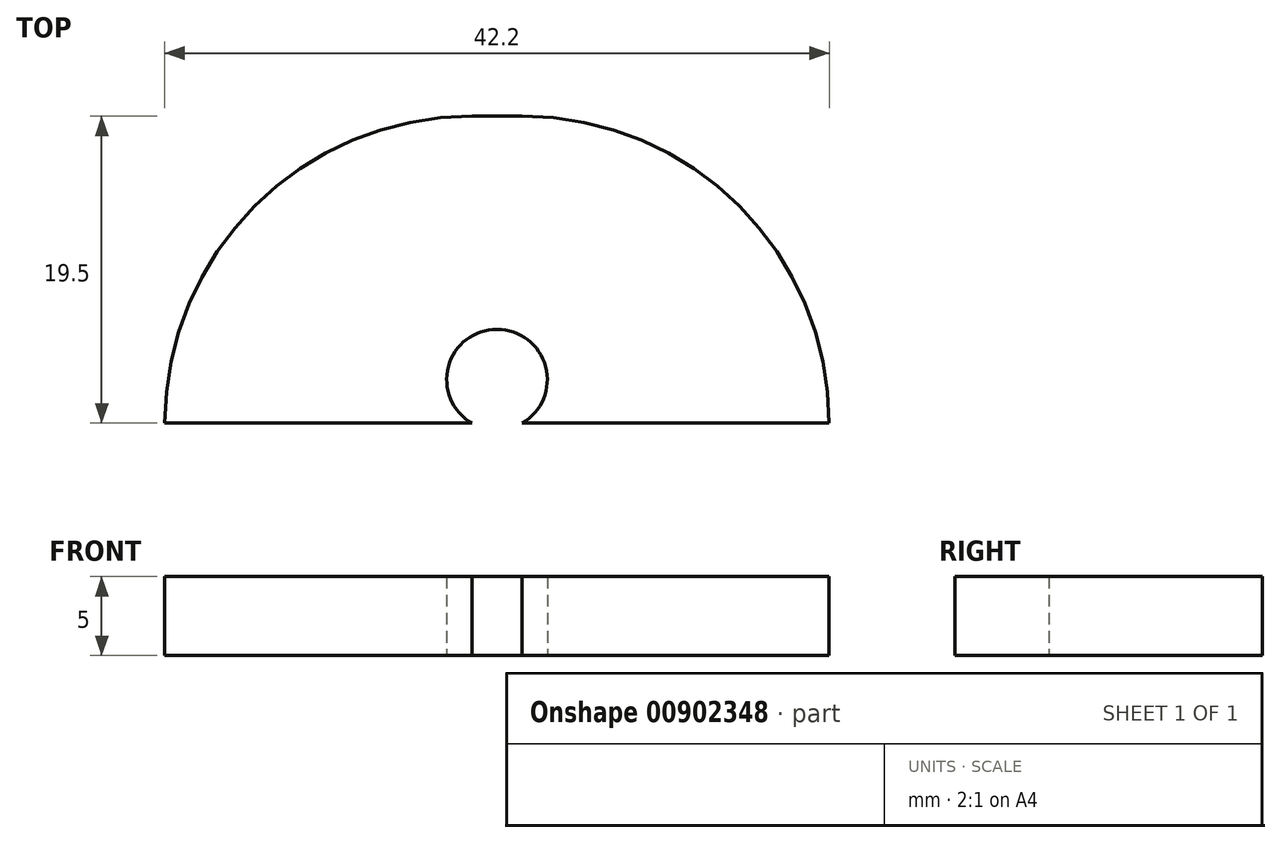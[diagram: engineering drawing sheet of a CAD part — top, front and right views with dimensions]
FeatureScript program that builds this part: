
annotation { "Feature Type Name" : "Feature", "Feature Type Description" : "" }
export const myFeature = defineFeature(function(context is Context, id is Id, definition is map)
    precondition{}
    {
        {
            var Q0;
            Q0=qCreatedBy(makeId("Top.planeOp"),FACE);
            var sketch = newSketch(context, id + "F0", { "sketchPlane" : qUnion([Q0])});
            skLineSegment(sketch, "E0.bottom", {"start": v(1.6, -9.75) * mm, "end": v(-1.6, -9.75) * mm});
            skLineSegment(sketch, "E0.top", {"start": v(1.6, 9.75) * mm, "end": v(-1.6, 9.75) * mm});
            skLineSegment(sketch, "E0.left", {"start": v(1.6, -9.75) * mm, "end": v(1.6, 9.75) * mm});
            skLineSegment(sketch, "E0.right", {"start": v(-1.6, -9.75) * mm, "end": v(-1.6, 9.75) * mm});
            skPoint(sketch, "E0.middle", {"position": v(0, 0) * mm});
            skCircle(sketch, "E1", {"center": v(1.6, -9.75) * mm, "radius": 19.5 * mm});
            skCircle(sketch, "E2", {"center": v(-1.6, -9.75) * mm, "radius": 19.5 * mm});
            skLineSegment(sketch, "E3", {"start": v(12.38, -9.75) * mm, "end": v(21.1, -9.75) * mm});
            skLineSegment(sketch, "E4", {"start": v(21.1, -9.75) * mm, "end": v(-21.1, -9.75) * mm});
            skLineSegment(sketch, "E5", {"start": v(-1.6, -9.75) * mm, "end": v(-1.6, -35.21) * mm});
            skLineSegment(sketch, "E6", {"start": v(1.6, -9.75) * mm, "end": v(1.6, -35.21) * mm});
            skLineSegment(sketch, "E7", {"start": v(21.1, -9.75) * mm, "end": v(69.98, -9.75) * mm});
            skLineSegment(sketch, "E8", {"start": v(69.98, -9.75) * mm, "end": v(-43.53, -9.75) * mm});
            skCircle(sketch, "E9", {"center": v(1.6, -9.75) * mm, "radius": 3.2 * mm});
            skCircle(sketch, "E10", {"center": v(-1.6, -9.75) * mm, "radius": 3.2 * mm});
            skCircle(sketch, "E11", {"center": v(0, -6.98) * mm, "radius": 3.2 * mm});
            skSolve(sketch);
        }
        {
            var Q0;
            {var subQ1=sQuery(id+"F0.wireOp",EDGE,"E0.right");var subQ3=sQuery(id+"F0.wireOp",EDGE,"E1");var subQ4=makeQuery(id+"F0.imprint","INTERSECT",VERTEX,{"derivedFrom":[subQ1,subQ3]});Q0=makeQuery(id+"F0.imprint","IMPRINT",FACE,{"disambiguationData":[TD([[makeQuery(id+"F0.imprint","IMPRINT",EDGE,{"disambiguationData":[TD([[subQ4,-1.0]])],"derivedFrom":subQ3}),-1.0]])]});}
            var Q1;
            {var subQ3=sQuery(id+"F0.wireOp",EDGE,"E11");var subQ7=sQuery(id+"F0.wireOp",EDGE,"E0.right");var subQ8=makeQuery(id+"F0.imprint","INTERSECT",VERTEX,{"derivedFrom":[subQ7,subQ3]});Q1=makeQuery(id+"F0.imprint","IMPRINT",FACE,{"disambiguationData":[TD([[makeQuery(id+"F0.imprint","IMPRINT",EDGE,{"disambiguationData":[TD([[subQ8,-1.0]])],"derivedFrom":subQ7}),1.0]])]});}
            var Q2;
            {var subQ1=sQuery(id+"F0.wireOp",EDGE,"E0.left");var subQ3=sQuery(id+"F0.wireOp",EDGE,"E2");var subQ4=makeQuery(id+"F0.imprint","INTERSECT",VERTEX,{"derivedFrom":[subQ1,subQ3]});Q2=makeQuery(id+"F0.imprint","IMPRINT",FACE,{"disambiguationData":[TD([[makeQuery(id+"F0.imprint","IMPRINT",EDGE,{"disambiguationData":[TD([[subQ4,1.0]])],"derivedFrom":subQ3}),-1.0]])]});}
            var Q3;
            {var subQ6=sQuery(id+"F0.wireOp",EDGE,"E0.left");var subQ9=sQuery(id+"F0.wireOp",EDGE,"E11");var subQ10=makeQuery(id+"F0.imprint","INTERSECT",VERTEX,{"derivedFrom":[subQ6,subQ9]});Q3=makeQuery(id+"F0.imprint","IMPRINT",FACE,{"disambiguationData":[TD([[makeQuery(id+"F0.imprint","IMPRINT",EDGE,{"disambiguationData":[TD([[subQ10,-1.0]])],"derivedFrom":subQ6}),-1.0]])]});}
            var Q4;
            {var subQ1=sQuery(id+"F0.wireOp",EDGE,"E4");var subQ3=sQuery(id+"F0.wireOp",EDGE,"E9");var subQ4=makeQuery(id+"F0.imprint","INTERSECT",VERTEX,{"derivedFrom":[subQ1,subQ3]});Q4=makeQuery(id+"F0.imprint","IMPRINT",FACE,{"disambiguationData":[TD([[makeQuery(id+"F0.imprint","IMPRINT",EDGE,{"disambiguationData":[TD([[subQ4,-1.0]])],"derivedFrom":subQ3}),1.0]])]});}
            var Q5;
            {var subQ1=sQuery(id+"F0.wireOp",EDGE,"E4");var subQ3=sQuery(id+"F0.wireOp",EDGE,"E10");var subQ4=makeQuery(id+"F0.imprint","INTERSECT",VERTEX,{"derivedFrom":[subQ1,subQ3]});Q5=makeQuery(id+"F0.imprint","IMPRINT",FACE,{"disambiguationData":[TD([[makeQuery(id+"F0.imprint","IMPRINT",EDGE,{"disambiguationData":[TD([[subQ4,1.0]])],"derivedFrom":subQ3}),1.0]])]});}
            var Q6;
            {var subQ1=sQuery(id+"F0.wireOp",EDGE,"E0.left");var subQ3=sQuery(id+"F0.wireOp",EDGE,"E2");var subQ4=makeQuery(id+"F0.imprint","INTERSECT",VERTEX,{"derivedFrom":[subQ1,subQ3]});Q6=makeQuery(id+"F0.imprint","IMPRINT",FACE,{"disambiguationData":[TD([[makeQuery(id+"F0.imprint","IMPRINT",EDGE,{"disambiguationData":[TD([[subQ4,-1.0]])],"derivedFrom":subQ3}),-1.0]])]});}
            var Q7;
            {var subQ1=sQuery(id+"F0.wireOp",EDGE,"E0.right");var subQ3=sQuery(id+"F0.wireOp",EDGE,"E1");var subQ4=makeQuery(id+"F0.imprint","INTERSECT",VERTEX,{"derivedFrom":[subQ1,subQ3]});Q7=makeQuery(id+"F0.imprint","IMPRINT",FACE,{"disambiguationData":[TD([[makeQuery(id+"F0.imprint","IMPRINT",EDGE,{"disambiguationData":[TD([[subQ4,1.0]])],"derivedFrom":subQ3}),-1.0]])]});}
            var Q8;
            {var subQ1=sQuery(id+"F0.wireOp",EDGE,"E0.left");var subQ5=sQuery(id+"F0.wireOp",EDGE,"E11");var subQ9=makeQuery(id+"F0.imprint","INTERSECT",VERTEX,{"derivedFrom":[subQ1,subQ5]});Q8=makeQuery(id+"F0.imprint","IMPRINT",FACE,{"disambiguationData":[TD([[makeQuery(id+"F0.imprint","IMPRINT",EDGE,{"disambiguationData":[TD([[subQ9,-1.0]])],"derivedFrom":subQ1}),1.0]])]});}
            var Q9;
            {var subQ0=sQuery(id+"F0.wireOp",EDGE,"E0.top");Q9=makeQuery(id+"F0.imprint","IMPRINT",FACE,{"disambiguationData":[TD([[makeQuery(id+"F0.imprint","IMPRINT",EDGE,{"derivedFrom":subQ0}),1.0]])]});}
            extrude(context, id + "F1", {"entities" : qUnion([Q0, Q1, Q2, Q3, Q4, Q5, Q6, Q7, Q8, Q9]), "depth" : 5 * mm, "offsetDistance" : 25 * mm});
        }
    });
